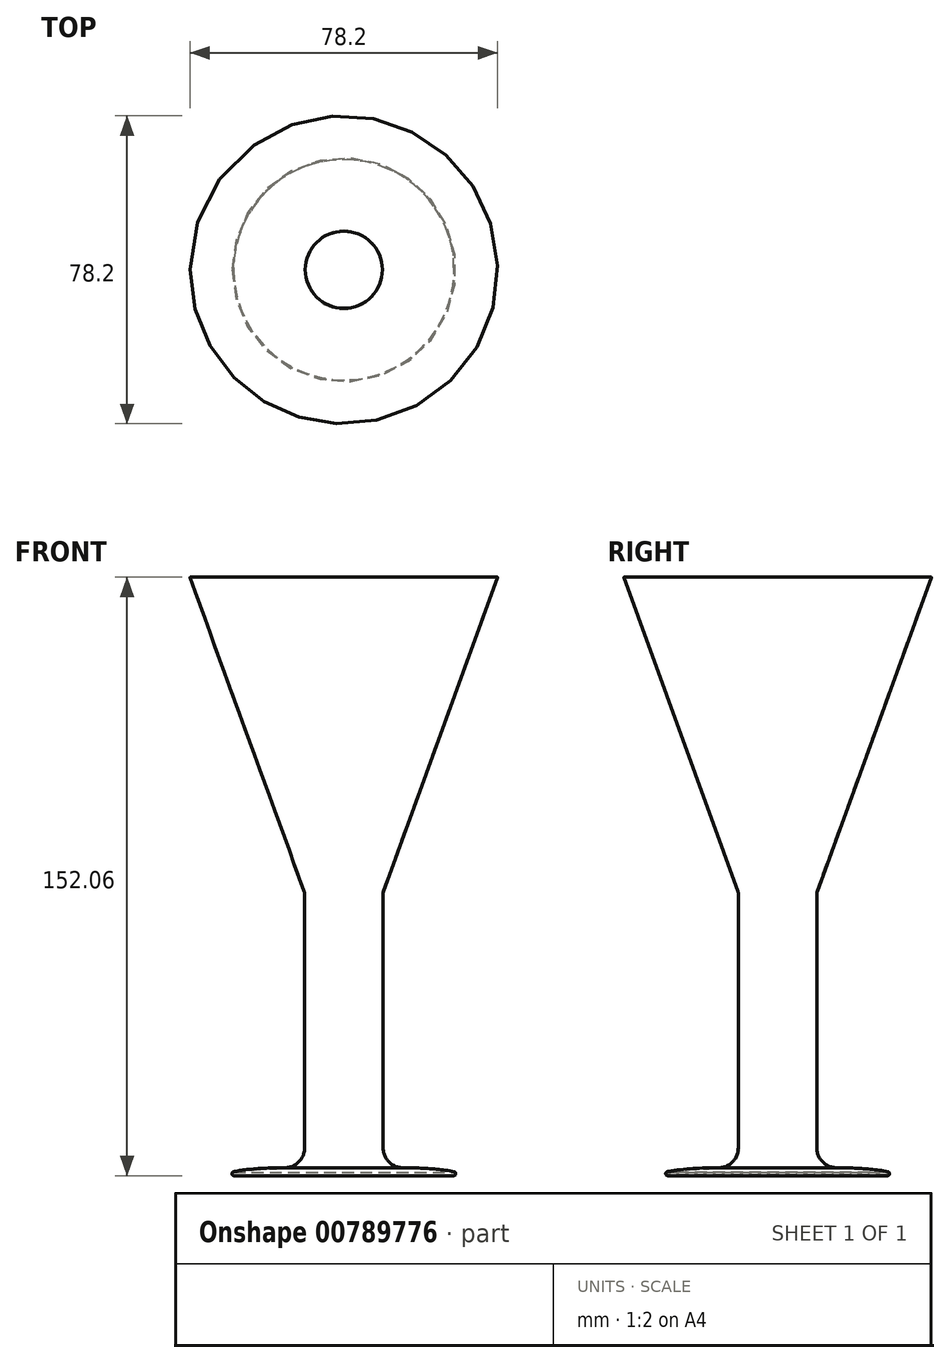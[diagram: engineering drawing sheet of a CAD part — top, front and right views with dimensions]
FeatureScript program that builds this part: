
annotation { "Feature Type Name" : "Feature", "Feature Type Description" : "" }
export const myFeature = defineFeature(function(context is Context, id is Id, definition is map)
    precondition{}
    {
        {
            var Q0;
            Q0=qCreatedBy(makeId("Front.planeOp"),FACE);
            var sketch = newSketch(context, id + "F0", { "sketchPlane" : qUnion([Q0])});
            skLineSegment(sketch, "E0", {"start": v(0, 0) * mm, "end": v(27.93, 0) * mm});
            skLineSegment(sketch, "E1", {"start": v(30, 0) * mm, "end": v(30, 2) * mm});
            skLineSegment(sketch, "E2", {"start": v(30, 2) * mm, "end": v(15, 2) * mm});
            skLineSegment(sketch, "E3", {"start": v(10, 7) * mm, "end": v(10, 71.82) * mm});
            skLineSegment(sketch, "E4", {"start": v(10.06, 72.17) * mm, "end": v(39.1, 151.93) * mm});
            skLineSegment(sketch, "E5", {"start": v(10, 72) * mm, "end": v(48.04, 72) * mm, "construction": true});
            skEllipticalArc(sketch, "E6", {});
            skPoint(sketch, "E7", {"position": v(10, 7) * mm});
            skArc(sketch, "E8.filletArc", {"start": v(10, 7) * mm, "mid": v(11.46, 3.46) * mm, "end": v(15, 2) * mm});
            skPoint(sketch, "E9.visualSharp", {"position": v(30, 0) * mm});
            skArc(sketch, "E10.filletArc", {"start": v(27.93, 0) * mm, "mid": v(28.43, 0.44) * mm, "end": v(28.05, 0.99) * mm});
            skArc(sketch, "E11.0", {"start": v(9.8, 7) * mm, "mid": v(11.32, 3.32) * mm, "end": v(15, 1.8) * mm});
            skFitSpline(sketch, "E11.1", {"points": [v(28, 0.8) * mm, v(27.36, 0.94) * mm, v(26.16, 1.15) * mm, v(24.2, 1.39) * mm, v(22.56, 1.53) * mm, v(20.78, 1.65) * mm, v(18.3, 1.76) * mm, v(16.32, 1.8) * mm, v(15, 1.8) * mm]});
            skArc(sketch, "E11.2", {"start": v(27.93, 0.2) * mm, "mid": v(28.23, 0.47) * mm, "end": v(28, 0.8) * mm});
            skLineSegment(sketch, "E11.3", {"start": v(0, 0.2) * mm, "end": v(27.93, 0.2) * mm});
            skLineSegment(sketch, "E12.0", {"start": v(9.8, 7) * mm, "end": v(9.8, 71.86) * mm});
            skLineSegment(sketch, "E13.2", {"start": v(9.86, 72.2) * mm, "end": v(38.9, 152) * mm});
            skLineSegment(sketch, "E14", {"start": v(0, 0) * mm, "end": v(0, 0.2) * mm});
            skArc(sketch, "E15", {"start": v(39.1, 151.93) * mm, "mid": v(39.03, 152.06) * mm, "end": v(38.9, 152) * mm});
            skPoint(sketch, "E15.second.point", {"position": v(39.1, 151.93) * mm});
            skPoint(sketch, "E15.third.point", {"position": v(39, 152.06) * mm});
            skLineSegment(sketch, "E16", {"start": v(0, 0.2) * mm, "end": v(0, 177.93) * mm, "construction": true});
            skPoint(sketch, "E17.visualSharp", {"position": v(10, 72) * mm});
            skArc(sketch, "E17.filletArc", {"start": v(10.06, 72.17) * mm, "mid": v(10.02, 72) * mm, "end": v(10, 71.82) * mm});
            skArc(sketch, "E18.filletArc", {"start": v(9.86, 72.2) * mm, "mid": v(9.82, 72.03) * mm, "end": v(9.8, 71.86) * mm});
            const initialGuessF0  = {"E6": [0.015, 0, -1, 0, 0.015, 0.002, 3.657548377476383, 4.71238898038469]};
            skSetInitialGuess(sketch, initialGuessF0);
            skSolve(sketch);
        }
        {
            var Q0;
            Q0=makeQuery(id+"F0.imprint","IMPRINT",FACE,{"disambiguationData":[TD([[makeQuery(id+"F0.imprint","IMPRINT",EDGE,{"derivedFrom":sQuery(id+"F0.wireOp",EDGE,"E0")}),1.0]])]});
            var Q1;
            Q1=sQuery(id+"F0.wireOp",EDGE,"E16");
            revolve(context, id + "F1", {"surfaceOperationType" : NewSurfaceOperationType.NEW, "entities" : qUnion([Q0]), "axis" : qUnion([Q1]), "revolveType" : RevolveType.FULL});
        }
    });
